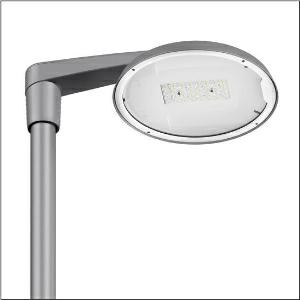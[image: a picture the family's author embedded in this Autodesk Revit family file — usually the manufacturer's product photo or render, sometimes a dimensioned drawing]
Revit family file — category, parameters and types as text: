
# Revit family: dl_r__50_iq_mini___st0_5a_5xa248b41f08je_3ec1
name_source: partatom
category: Lighting Fixtures
units: mm (PartAtom-declared; Revit-internal decimal feet)

## family parameters
Cut with Voids When Loaded = No
Host = Face
Light Source = No
Part Type = Normal
Room Calculation Point = No
Round Connector Dimension = Use Diameter
Shared = No

## types (1)
- --- (1 x LED, 10300 lm, 62.6 W, 4000K)
    Apparent Load = 63 VA
    CIE Flux Codes = 43 76 97 100 100
    Color Rendering = 70
    Color Temperature = 4000K
    Default Elevation = 1800 mm
    Description = DL® 50 iQ mini, mast luminaire, primary light control with lens, of PMMA, primary optical cover: cover, of toughened safety glass, transparent, light distribution: ST0.5a, light emission: direct distribution, primary light characteristic: asymmetric, installation type: side-entry, post-top, LED, High Power LED, rated luminous flux: 10.300lm, luminous efficacy: 165lm/W, light colour: 740, colour temperature: 4000K, control: optimised constant luminous flux control (CLO 2.0), Desk-Remote (wireless, voltage-free reading and setting of iQ features in the workshop via application-optimized NFC function/RFID function), Light-Fading, Smart-Wire, Night-Set, Lumen-Switch, Temp-Guard, Auto-Match, Street-Remote, mains connection: 230..240V, AC, 50/60Hz, connection cable pre-assembled, cable length: 8,5m, start of lifetime: 63W, end of service life: 65W, reduction: 29W, luminaire housing, of diecast aluminium, powder-coated, Siteco® metallic grey (DB 702S), inclination adjustable: 0°, 5°, 10° (post-top) | 0°, -5°, -10°, -15° (side-entry), please order mast post-top element or mast side-entry element separately, diameter: 500mm, height: 115mm, post-top: for spigot size d x l = 76 x 100mm; with reducer (optional accessory) 60 x 100mm | side-entry: for spigot size d x l = 60 x 100mm; with reducer (optional accessory) 42 x 100mm, protection rating (complete): IP66, insulation class (complete): insulation class II (safety insulation), certification: CE, ENEC, ENEC+, VDE, impact resistance: IK08, permissible operating ambient temperature for outdoor applications: -25..+40°C, standard-compliant lighting for roads and squares, packaging unit: 1 piece

Light Distribution: ST0.5a
    Height = 115 mm
    Lamp = 1 x LED
    Lamp Light Flux = 10300 lm
    Lamp Power = 62.6 W
    Lamp count = 1
    Length = 500 mm
    Luminous efficacy = 165 lm/W
    Manufacturer = Siteco
    ModVariant = No
    Model = 5XA248B41F08JE
    Number of Poles = 1
    OnlyDefault = Yes
    Power Factor = 1
    Product Name = DL® 50 iQ mini | ST0.5a
    Product group = mast luminaire | pylon top
    ProductGroupID = 6100
    Protection Class = Protection class II
    Protection Degree = IP 66
    RLX_Detail_Level = 1
    RLX_Emergency_Light_Flux = 0 lm
    RLX_Emergency_Type = 0
    RLX_Emergency_Type_DB = No
    RlxData = <blob elided: 127285 chars, md5=73a8bd23>
    Socket = socket
    Standby Power = 0 W
    System Light Flux = 10300 lm
    System Power = 63 W
    Type Comments = factory setting: luminous flux: 100 % | dim-lin: 254 | 658 mA
    Type Image = l_1251794.jpg
    URL = http://relux.com
    VarID = @adj_112685
    Voltage = 0 V
    Weight = 0.00 kg
    Width = 0 mm  [stored 0 ft]

note: [stored X ft] marks values corroborated as IEEE doubles in the binary element streams (Revit-internal decimal feet)

## geometry (parser evidence)
native form markers: Blend x4, Sweep x12
no freeform markers — native parametric forms only
